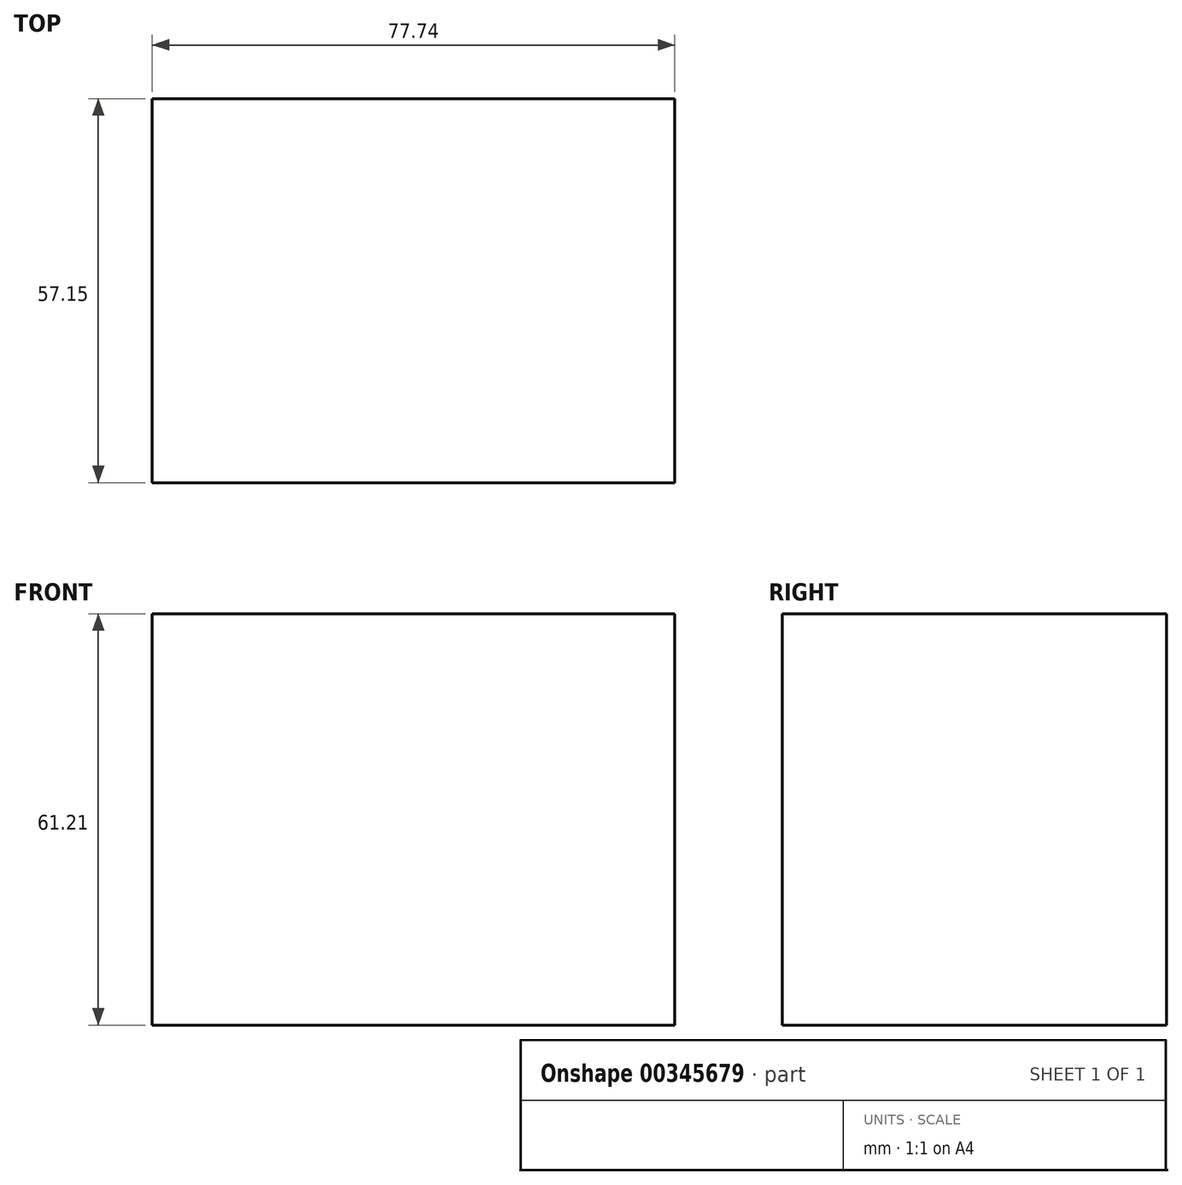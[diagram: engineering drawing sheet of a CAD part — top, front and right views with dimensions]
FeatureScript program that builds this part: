
annotation { "Feature Type Name" : "Feature", "Feature Type Description" : "" }
export const myFeature = defineFeature(function(context is Context, id is Id, definition is map)
    precondition{}
    {
        {
            var Q0;
            Q0=qCreatedBy(makeId("Top.planeOp"),FACE);
            var sketch = newSketch(context, id + "F0", { "sketchPlane" : qUnion([Q0])});
            skLineSegment(sketch, "E0.bottom", {"start": v(41.56, -34.42) * mm, "end": v(-36.18, -34.42) * mm});
            skLineSegment(sketch, "E0.top", {"start": v(41.56, 22.73) * mm, "end": v(-36.18, 22.73) * mm});
            skLineSegment(sketch, "E0.left", {"start": v(41.56, -34.42) * mm, "end": v(41.56, 22.73) * mm});
            skLineSegment(sketch, "E0.right", {"start": v(-36.18, -34.42) * mm, "end": v(-36.18, 22.73) * mm});
            skSolve(sketch);
        }
        {
            var Q0;
            Q0 = qSketchRegion(id + "F0", true);
            extrude(context, id + "F1", {"entities" : qUnion([Q0]), "oppositeDirection" : true, "depth" : 61.2 * mm});
        }
    });
